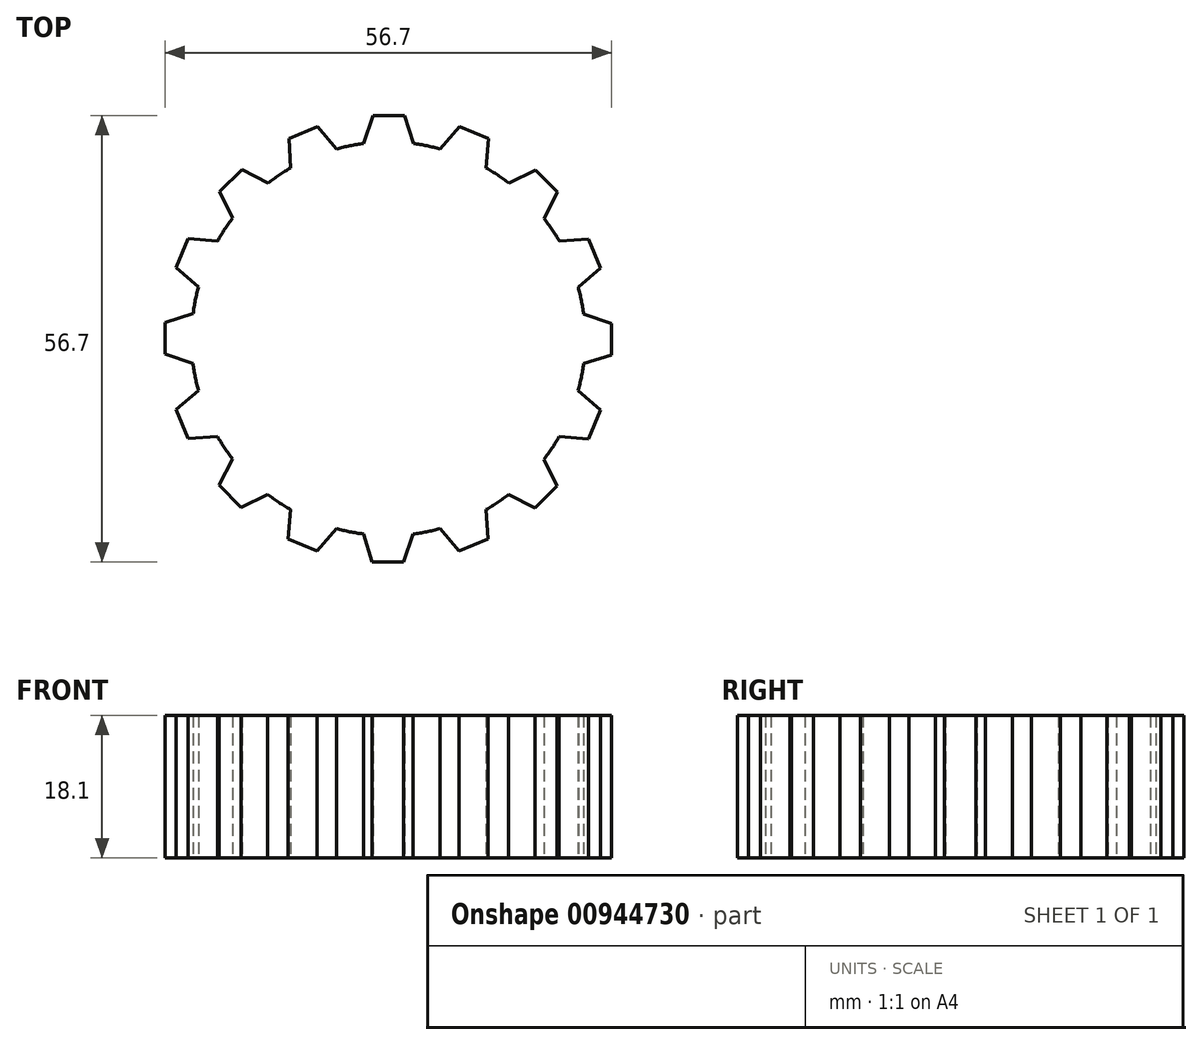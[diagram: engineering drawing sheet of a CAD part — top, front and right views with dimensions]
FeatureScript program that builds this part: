
annotation { "Feature Type Name" : "Feature", "Feature Type Description" : "" }
export const myFeature = defineFeature(function(context is Context, id is Id, definition is map)
    precondition{}
    {
        {
            var Q0;
            Q0=qCreatedBy(makeId("Top.planeOp"),FACE);
            var sketch = newSketch(context, id + "F0", { "sketchPlane" : qUnion([Q0])});
            skCircle(sketch, "E0", {"center": v(0, 0) * mm, "radius": 25 * mm});
            skLineSegment(sketch, "E1", {"start": v(-3.14, 24.8) * mm, "end": v(-1.94, 28.35) * mm});
            skLineSegment(sketch, "E2", {"start": v(-1.94, 28.35) * mm, "end": v(2.04, 28.35) * mm});
            skLineSegment(sketch, "E3", {"start": v(2.04, 28.35) * mm, "end": v(3.18, 24.8) * mm});
            skLineSegment(sketch, "E4.1.0", {"start": v(-12.4, 21.71) * mm, "end": v(-12.64, 25.45) * mm});
            skLineSegment(sketch, "E4.1.1", {"start": v(-12.64, 25.45) * mm, "end": v(-8.96, 26.98) * mm});
            skLineSegment(sketch, "E4.1.2", {"start": v(-8.96, 26.98) * mm, "end": v(-6.55, 24.13) * mm});
            skLineSegment(sketch, "E4.2.0", {"start": v(-19.76, 15.32) * mm, "end": v(-21.42, 18.68) * mm});
            skLineSegment(sketch, "E4.2.1", {"start": v(-21.42, 18.68) * mm, "end": v(-18.6, 21.5) * mm});
            skLineSegment(sketch, "E4.2.2", {"start": v(-18.6, 21.5) * mm, "end": v(-15.29, 19.78) * mm});
            skLineSegment(sketch, "E4.3.0", {"start": v(-24.12, 6.6) * mm, "end": v(-26.94, 9.06) * mm});
            skLineSegment(sketch, "E4.3.1", {"start": v(-26.94, 9.06) * mm, "end": v(-25.41, 12.74) * mm});
            skLineSegment(sketch, "E4.3.2", {"start": v(-25.41, 12.74) * mm, "end": v(-21.7, 12.42) * mm});
            skLineSegment(sketch, "E4.4.0", {"start": v(-24.8, -3.14) * mm, "end": v(-28.35, -1.94) * mm});
            skLineSegment(sketch, "E4.4.1", {"start": v(-28.35, -1.94) * mm, "end": v(-28.35, 2.04) * mm});
            skLineSegment(sketch, "E4.4.2", {"start": v(-28.35, 2.04) * mm, "end": v(-24.8, 3.18) * mm});
            skLineSegment(sketch, "E4.5.0", {"start": v(-21.71, -12.4) * mm, "end": v(-25.45, -12.64) * mm});
            skLineSegment(sketch, "E4.5.1", {"start": v(-25.45, -12.64) * mm, "end": v(-26.98, -8.96) * mm});
            skLineSegment(sketch, "E4.5.2", {"start": v(-26.98, -8.96) * mm, "end": v(-24.13, -6.55) * mm});
            skLineSegment(sketch, "E4.6.0", {"start": v(-15.32, -19.76) * mm, "end": v(-18.68, -21.42) * mm});
            skLineSegment(sketch, "E4.6.1", {"start": v(-18.68, -21.42) * mm, "end": v(-21.5, -18.6) * mm});
            skLineSegment(sketch, "E4.6.2", {"start": v(-21.5, -18.6) * mm, "end": v(-19.78, -15.29) * mm});
            skLineSegment(sketch, "E4.7.0", {"start": v(-6.6, -24.12) * mm, "end": v(-9.06, -26.94) * mm});
            skLineSegment(sketch, "E4.7.1", {"start": v(-9.06, -26.94) * mm, "end": v(-12.74, -25.41) * mm});
            skLineSegment(sketch, "E4.7.2", {"start": v(-12.74, -25.41) * mm, "end": v(-12.42, -21.7) * mm});
            skLineSegment(sketch, "E4.8.0", {"start": v(3.14, -24.8) * mm, "end": v(1.94, -28.35) * mm});
            skLineSegment(sketch, "E4.8.1", {"start": v(1.94, -28.35) * mm, "end": v(-2.04, -28.35) * mm});
            skLineSegment(sketch, "E4.8.2", {"start": v(-2.04, -28.35) * mm, "end": v(-3.18, -24.8) * mm});
            skLineSegment(sketch, "E4.9.0", {"start": v(12.4, -21.71) * mm, "end": v(12.64, -25.45) * mm});
            skLineSegment(sketch, "E4.9.1", {"start": v(12.64, -25.45) * mm, "end": v(8.96, -26.98) * mm});
            skLineSegment(sketch, "E4.9.2", {"start": v(8.96, -26.98) * mm, "end": v(6.55, -24.13) * mm});
            skLineSegment(sketch, "E4.10.0", {"start": v(19.76, -15.32) * mm, "end": v(21.42, -18.68) * mm});
            skLineSegment(sketch, "E4.10.1", {"start": v(21.42, -18.68) * mm, "end": v(18.6, -21.5) * mm});
            skLineSegment(sketch, "E4.10.2", {"start": v(18.6, -21.5) * mm, "end": v(15.29, -19.78) * mm});
            skLineSegment(sketch, "E4.11.0", {"start": v(24.12, -6.6) * mm, "end": v(26.94, -9.06) * mm});
            skLineSegment(sketch, "E4.11.1", {"start": v(26.94, -9.06) * mm, "end": v(25.41, -12.74) * mm});
            skLineSegment(sketch, "E4.11.2", {"start": v(25.41, -12.74) * mm, "end": v(21.7, -12.42) * mm});
            skLineSegment(sketch, "E4.12.0", {"start": v(24.8, 3.14) * mm, "end": v(28.35, 1.94) * mm});
            skLineSegment(sketch, "E4.12.1", {"start": v(28.35, 1.94) * mm, "end": v(28.35, -2.04) * mm});
            skLineSegment(sketch, "E4.12.2", {"start": v(28.35, -2.04) * mm, "end": v(24.8, -3.18) * mm});
            skLineSegment(sketch, "E4.13.0", {"start": v(21.71, 12.4) * mm, "end": v(25.45, 12.64) * mm});
            skLineSegment(sketch, "E4.13.1", {"start": v(25.45, 12.64) * mm, "end": v(26.98, 8.96) * mm});
            skLineSegment(sketch, "E4.13.2", {"start": v(26.98, 8.96) * mm, "end": v(24.13, 6.55) * mm});
            skLineSegment(sketch, "E4.14.0", {"start": v(15.32, 19.76) * mm, "end": v(18.68, 21.42) * mm});
            skLineSegment(sketch, "E4.14.1", {"start": v(18.68, 21.42) * mm, "end": v(21.5, 18.6) * mm});
            skLineSegment(sketch, "E4.14.2", {"start": v(21.5, 18.6) * mm, "end": v(19.78, 15.29) * mm});
            skLineSegment(sketch, "E4.15.0", {"start": v(6.6, 24.12) * mm, "end": v(9.06, 26.94) * mm});
            skLineSegment(sketch, "E4.15.1", {"start": v(9.06, 26.94) * mm, "end": v(12.74, 25.41) * mm});
            skLineSegment(sketch, "E4.15.2", {"start": v(12.74, 25.41) * mm, "end": v(12.42, 21.7) * mm});
            skSolve(sketch);
        }
        {
            var Q0;
            Q0 = qSketchRegion(id + "F0", true);
            extrude(context, id + "F1", {"entities" : qUnion([Q0]), "depth" : 18.1 * mm, "offsetDistance" : 25 * mm});
        }
    });
